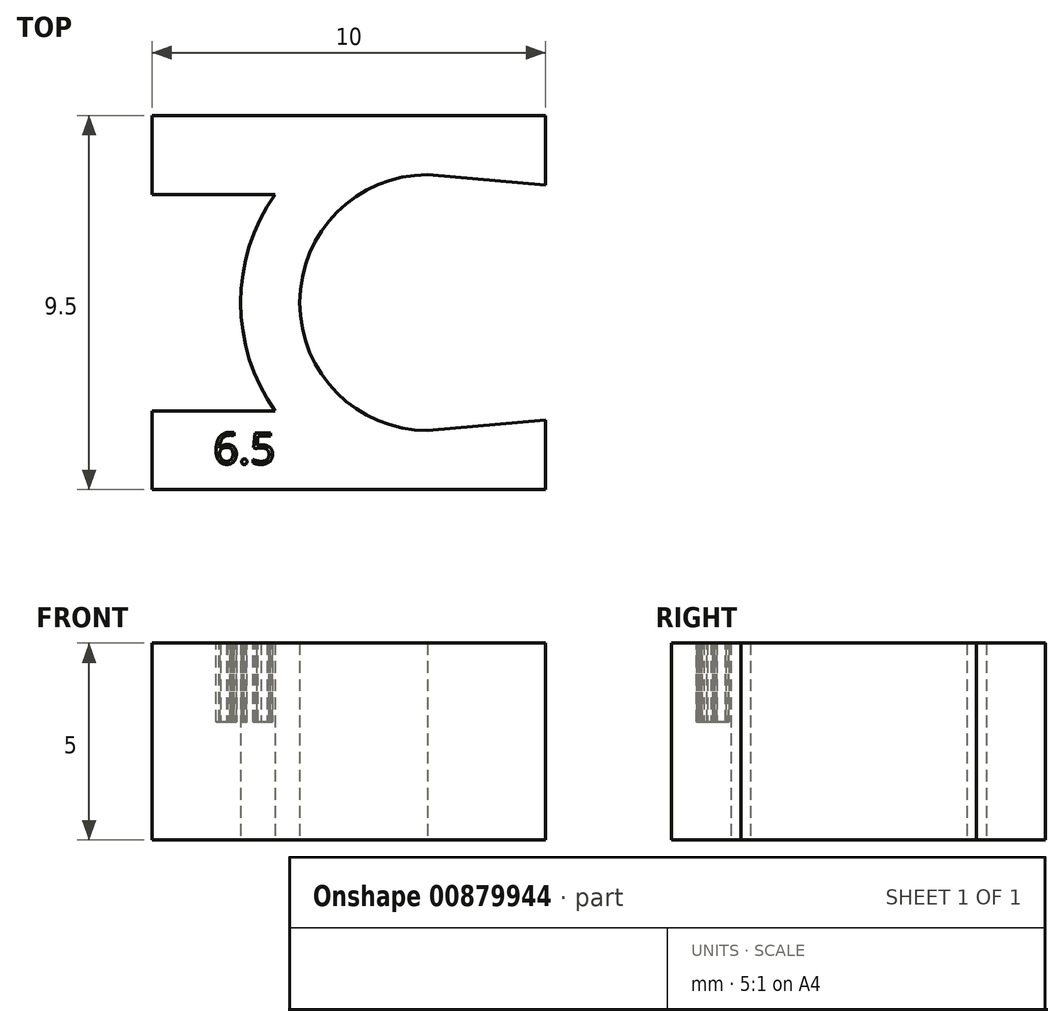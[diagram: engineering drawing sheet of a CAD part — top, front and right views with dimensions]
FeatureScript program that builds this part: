
annotation { "Feature Type Name" : "Feature", "Feature Type Description" : "" }
export const myFeature = defineFeature(function(context is Context, id is Id, definition is map)
    precondition{}
    {
        {
            var Q0;
            Q0=qCreatedBy(makeId("Top.planeOp"),FACE);
            var sketch = newSketch(context, id + "F0", { "sketchPlane" : qUnion([Q0])});
            skArc(sketch, "E0", {"start": v(0, 3.25) * mm, "mid": v(-3.25, 0) * mm, "end": v(0, -3.25) * mm});
            skArc(sketch, "E1", {"start": v(-3.87, 2.75) * mm, "mid": v(-4.75, 0) * mm, "end": v(-3.87, -2.75) * mm});
            skLineSegment(sketch, "E2", {"start": v(0, -4.75) * mm, "end": v(3, -4.75) * mm});
            skLineSegment(sketch, "E3", {"start": v(0, 4.75) * mm, "end": v(3, 4.75) * mm});
            skLineSegment(sketch, "E4", {"start": v(0, 3.25) * mm, "end": v(3, 2.99) * mm});
            skLineSegment(sketch, "E5", {"start": v(0, -3.25) * mm, "end": v(3, -2.99) * mm});
            skLineSegment(sketch, "E6", {"start": v(3, -2.99) * mm, "end": v(3, -4.75) * mm});
            skLineSegment(sketch, "E7", {"start": v(3, 4.75) * mm, "end": v(3, 2.99) * mm});
            skLineSegment(sketch, "E8", {"start": v(0, 4.75) * mm, "end": v(-7, 4.75) * mm});
            skLineSegment(sketch, "E9", {"start": v(-3.87, 2.75) * mm, "end": v(-7, 2.75) * mm});
            skLineSegment(sketch, "E10", {"start": v(0, -4.75) * mm, "end": v(-7, -4.75) * mm});
            skLineSegment(sketch, "E11", {"start": v(-3.87, -2.75) * mm, "end": v(-7, -2.75) * mm});
            skLineSegment(sketch, "E12", {"start": v(-7, -2.75) * mm, "end": v(-7, -4.75) * mm});
            skLineSegment(sketch, "E13", {"start": v(-7, 4.75) * mm, "end": v(-7, 2.75) * mm});
            skSolve(sketch);
        }
        {
            var Q0;
            Q0=makeQuery(id+"F0.imprint","IMPRINT",FACE,{"disambiguationData":[TD([[makeQuery(id+"F0.imprint","IMPRINT",EDGE,{"derivedFrom":sQuery(id+"F0.wireOp",EDGE,"E0")}),-1.0]])]});
            extrude(context, id + "F1", {"entities" : qUnion([Q0]), "depth" : 5 * mm, "offsetDistance" : 25 * mm});
        }
        {
            var Q0;
            Q0=makeQuery(id+"F1.opExtrude","CAP_FACE",FACE,{"disambiguationData":[OSD([sQuery(id+"F0.wireOp",EDGE,"E0"),sQuery(id+"F0.wireOp",EDGE,"E1"),sQuery(id+"F0.wireOp",EDGE,"E2"),sQuery(id+"F0.wireOp",EDGE,"E3"),sQuery(id+"F0.wireOp",EDGE,"E4"),sQuery(id+"F0.wireOp",EDGE,"E5"),sQuery(id+"F0.wireOp",EDGE,"E6"),sQuery(id+"F0.wireOp",EDGE,"E7"),sQuery(id+"F0.wireOp",EDGE,"E8"),sQuery(id+"F0.wireOp",EDGE,"E9"),sQuery(id+"F0.wireOp",EDGE,"E10"),sQuery(id+"F0.wireOp",EDGE,"E11"),sQuery(id+"F0.wireOp",EDGE,"E12"),sQuery(id+"F0.wireOp",EDGE,"E13")])],"isStart":false});
            var sketch = newSketch(context, id + "F2", { "sketchPlane" : qUnion([Q0])});
            skText(sketch, "E14", { "text": "6.5", "fontName": "OpenSans-Regular.ttf"});
            skPoint(sketch, "E14.firstSnap0", {"position": v(-5.44, -2.75) * mm});
            const initialGuessF2  = {"E14": [-0.00544, -0.0041, 1, 0, 0.0008]};
            skSetInitialGuess(sketch, initialGuessF2);
            skSolve(sketch);
        }
        {
            var Q0;
            Q0=makeQuery(id+"F2.imprint","IMPRINT",FACE,{"disambiguationData":[TD([[makeQuery(id+"F2.imprint","IMPRINT",EDGE,{"derivedFrom":sQuery(id+"F2.wireOp",EDGE,"E14.sketch_text.stroke-0")}),-1.0]])]});
            var Q1;
            Q1=makeQuery(id+"F2.imprint","IMPRINT",FACE,{"disambiguationData":[TD([[makeQuery(id+"F2.imprint","IMPRINT",EDGE,{"derivedFrom":sQuery(id+"F2.wireOp",EDGE,"E14.sketch_text.stroke-25")}),-1.0]])]});
            var Q2;
            Q2=makeQuery(id+"F2.imprint","IMPRINT",FACE,{"disambiguationData":[TD([[makeQuery(id+"F2.imprint","IMPRINT",EDGE,{"derivedFrom":sQuery(id+"F2.wireOp",EDGE,"E14.sketch_text.stroke-33")}),-1.0]])]});
            extrude(context, id + "F3", {"entities" : qUnion([Q0, Q1, Q2]), "operationType" : NewBodyOperationType.REMOVE, "oppositeDirection" : true, "depth" : 2 * mm, "offsetDistance" : 25 * mm});
        }
    });
